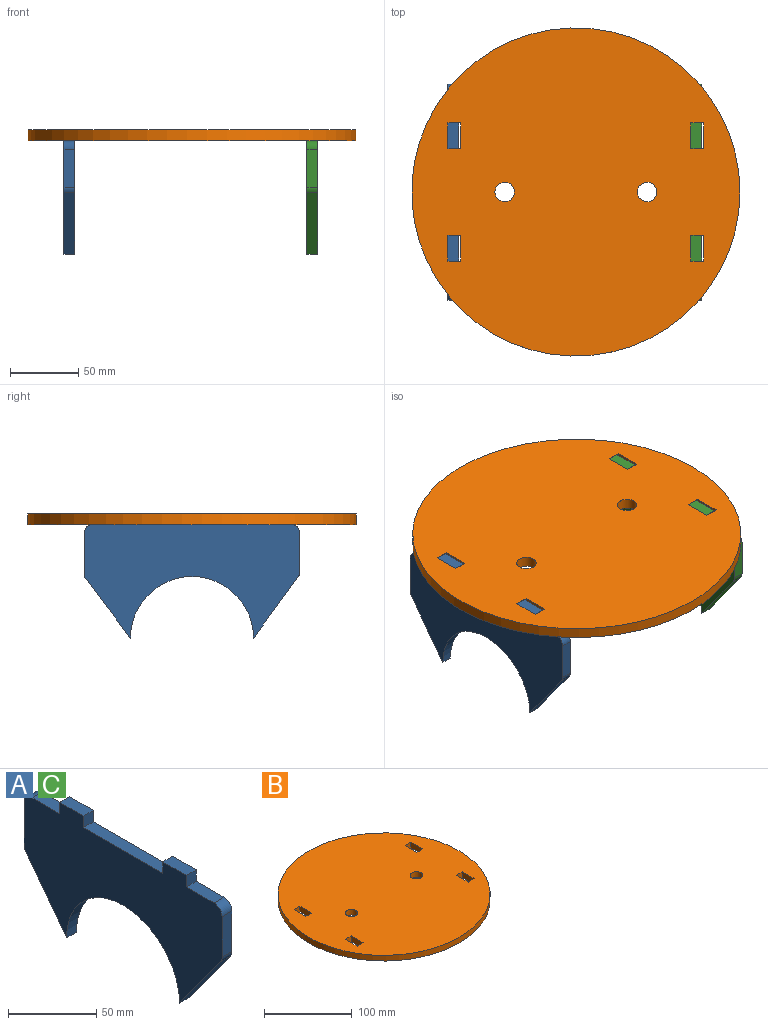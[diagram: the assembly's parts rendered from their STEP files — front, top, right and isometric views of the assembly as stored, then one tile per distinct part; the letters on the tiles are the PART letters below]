
ASSEMBLY  parts=3 mates=2
PART A: 20 faces, bbox 7.9x158.8x91.3 mm
  f0: plane 19.05x7.94mm, normal (0,0,1), area 151.2mm2, adj f1,f17,f18,f19
  f1: plane 7.94x7.94mm, normal (0,-1,0), area 63mm2, adj f0,f2,f18,f19
  f2: plane 22.23x7.94mm, normal (0,0,1), area 176.4mm2, adj f1,f3,f18,f19
  f3: cylinder r=6.35mm len=7.94mm, axis (-1,0,0), area 79.2mm2, adj f2,f4,f18,f19
  f4: plane 28.15x7.94mm, normal (0,-1,0), area 223.5mm2, adj f3,f5,f18,f19
  f5: cylinder r=6.35mm len=7.94mm, axis (-1,0,0), area 31.8mm2, adj f4,f6,f18,f19
  f6: plane 45.1x32.91mm, normal (0,-0.81,-0.59), area 443.1mm2, adj f5,f7,f18,f19
  f7: cylinder r=45.24mm len=90.49mm, axis (-1,0,0), area 1128.2mm2, adj f6,f8,f18,f19
  f8: plane 43.55x32.85mm, normal (0,0.8,-0.6), area 433mm2, adj f7,f9,f18,f19
  f9: cylinder r=6.35mm len=7.94mm, axis (-1,0,0), area 32.6mm2, adj f8,f10,f18,f19
  f10: plane 29.62x7.94mm, normal (0,1,0), area 235.1mm2, adj f9,f11,f18,f19
  f11: cylinder r=6.35mm len=7.94mm, axis (-1,0,0), area 79.2mm2, adj f10,f12,f18,f19
  f12: plane 22.23x7.94mm, normal (0,0,1), area 176.4mm2, adj f11,f13,f18,f19
  f13: plane 7.94x7.94mm, normal (0,1,0), area 63mm2, adj f12,f14,f18,f19
  f14: plane 19.05x7.94mm, normal (0,0,1), area 151.2mm2, adj f13,f15,f18,f19
  f15: plane 7.94x7.94mm, normal (0,-1,0), area 63mm2, adj f14,f16,f18,f19
  f16: plane 63.5x7.94mm, normal (0,0,1), area 504mm2, adj f15,f17,f18,f19
  f17: plane 7.94x7.94mm, normal (0,1,0), area 63mm2, adj f0,f16,f18,f19
  f18: plane 158.75x91.28mm, normal (1,0,0), area 8729.4mm2, adj f0,f1,f2,f3,f4,f5,f6,f7
  f19: plane 158.75x91.28mm, normal (-1,0,0), area 8729.4mm2, adj f0,f1,f2,f3,f4,f5,f6,f7
PART B: 21 faces, bbox 241.3x241.3x7.9 mm
  f0: plane 19.05x7.94mm, normal (1,0,0), area 151.2mm2, adj f1,f14,f19,f20
  f1: plane 9.53x7.94mm, normal (0,-1,0), area 75.6mm2, adj f0,f2,f19,f20
  f2: plane 19.05x7.94mm, normal (-1,0,0), area 151.2mm2, adj f1,f14,f19,f20
  f3: plane 19.05x7.94mm, normal (1,0,0), area 151.2mm2, adj f4,f15,f19,f20
  f4: plane 9.53x7.94mm, normal (0,-1,0), area 75.6mm2, adj f3,f5,f19,f20
  f5: plane 19.05x7.94mm, normal (-1,0,0), area 151.2mm2, adj f4,f15,f19,f20
  f6: plane 19.05x7.94mm, normal (1,0,0), area 151.2mm2, adj f7,f16,f19,f20
  f7: plane 9.53x7.94mm, normal (0,-1,0), area 75.6mm2, adj f6,f8,f19,f20
  f8: plane 19.05x7.94mm, normal (-1,0,0), area 151.2mm2, adj f7,f16,f19,f20
  f9: plane 19.05x7.94mm, normal (1,0,0), area 151.2mm2, adj f10,f17,f19,f20
  f10: plane 9.53x7.94mm, normal (0,-1,0), area 75.6mm2, adj f9,f11,f19,f20
  f11: plane 19.05x7.94mm, normal (-1,0,0), area 151.2mm2, adj f10,f17,f19,f20
  f12: cylinder r=7.14mm len=14.29mm, axis (0,0,-1), area 356.3mm2, adj f19,f20
  f13: cylinder r=7.14mm len=14.29mm, axis (0,0,-1), area 356.3mm2, adj f19,f20
  f14: plane 9.53x7.94mm, normal (0,1,0), area 75.6mm2, adj f0,f2,f19,f20
  f15: plane 9.53x7.94mm, normal (0,1,0), area 75.6mm2, adj f3,f5,f19,f20
  f16: plane 9.53x7.94mm, normal (0,1,0), area 75.6mm2, adj f6,f8,f19,f20
  f17: plane 9.53x7.94mm, normal (0,1,0), area 75.6mm2, adj f9,f11,f19,f20
  f18: cylinder r=120.65mm len=241.3mm, axis (0,0,-1), area 6017.2mm2, adj f19,f20
  f19: plane 241.3x241.3mm, normal (0,0,1), area 44683.9mm2, adj f0,f1,f2,f3,f4,f5,f6,f7
  f20: plane 241.3x241.3mm, normal (0,0,-1), area 44683.9mm2, adj f0,f1,f2,f3,f4,f5,f6,f7
PART C: same geometry as A
PLACE A t=(-94.03,0,-91.28)mm
PLACE B t=(0,0,-7.94)mm
PLACE C t=(84.5,0,-91.28)mm
MATE fastened B.f6 <-> B.f18  axis (1,0,0) through (-94.03,-50.8,0)mm
MATE fastened C.f19 <-> B.f0  axis (-1,0,0) through (84.5,-50.8,0)mm
